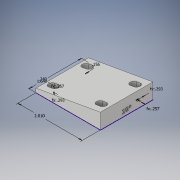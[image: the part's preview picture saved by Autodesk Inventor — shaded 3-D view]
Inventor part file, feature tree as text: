
AUTODESK INVENTOR PART (.ipt)
format: ipt  version: 2018 (Build 220112000, 112)  size: 205,312 bytes
history: native  units: in
note: dims shown in document units (in); Inventor stores cm internally (conversion verified against a paired STEP export)
features: sketch x4, extrude x3, projected_geometry x1
ambient origin geometry x8: Origin, YZ Plane, XZ Plane, XY Plane, X Axis, Y Axis, Z Axis, Center Point
bodies: Body1 (feature_tree)
feature tree (8):
  sketch  "Sketch1"  dims[d0=0.1562in d1=1.64in]
  extrude  "Extrusion8"  Depth=1.64in
  extrude  "Extrusion9"  Depth=0.24in
  extrude  "Extrusion10"  Depth=0.257in
  sketch  "Sketch10"  dims[d2=2.01in d3=0.24in]
  sketch  "Sketch11"  dims[d4=0.293in d5=0.257in]
  sketch  "Sketch13"  dims[d6=0.293in d7=0.257in d20=0.125in d21=1.25in d22=0.125in d23=0.125in d24=0.1875in d25=0.0938in d61=0.0687in d62=0.125in d63=1.64in d64=0.0in d65=0.125in d66=0.0995in d67=1.64in d68=0.0in d69=0.08in d70=0.015in d71=0.0in]
  projected_geometry  "Projected Loop1"
